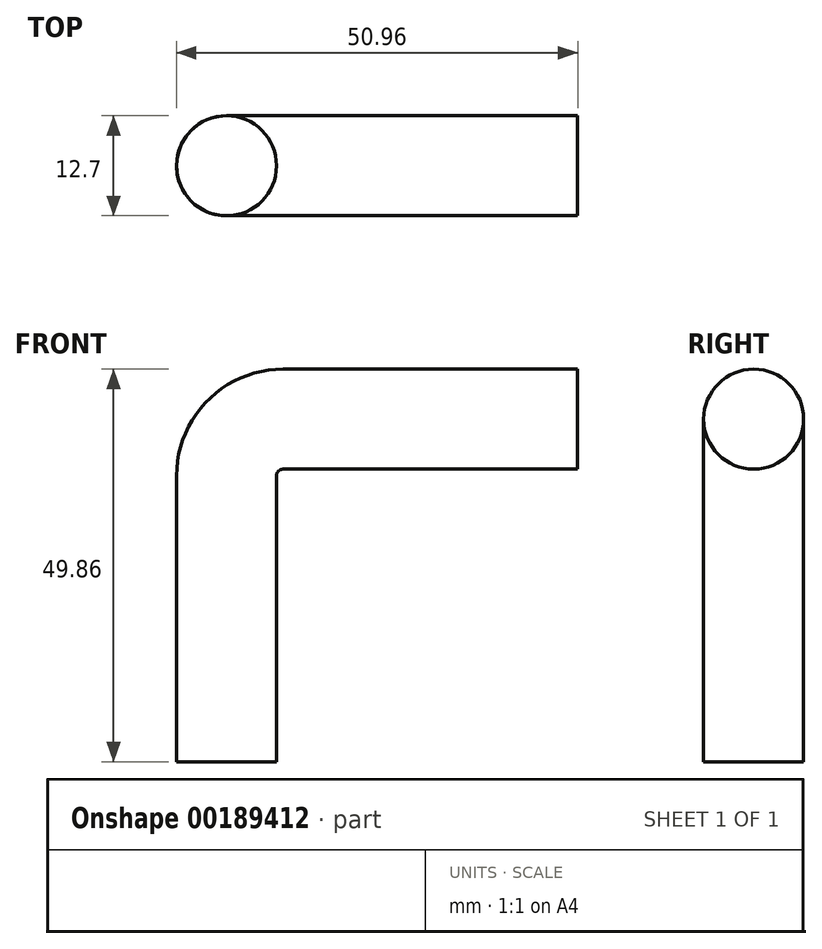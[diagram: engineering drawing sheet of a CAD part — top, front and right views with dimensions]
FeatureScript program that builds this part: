
annotation { "Feature Type Name" : "Feature", "Feature Type Description" : "" }
export const myFeature = defineFeature(function(context is Context, id is Id, definition is map)
    precondition{}
    {
        {
            var Q0;
            Q0=qCreatedBy(makeId("Top.planeOp"),FACE);
            var sketch = newSketch(context, id + "F0", { "sketchPlane" : qUnion([Q0])});
            skCircle(sketch, "E0", {"center": v(0, 0) * mm, "radius": 6.35 * mm});
            skSolve(sketch);
        }
        {
            var Q0;
            Q0=qCreatedBy(makeId("Front.planeOp"),FACE);
            var sketch = newSketch(context, id + "F1", { "sketchPlane" : qUnion([Q0])});
            skLineSegment(sketch, "E1", {"start": v(0, 0) * mm, "end": v(0, 36.34) * mm});
            skLineSegment(sketch, "E2", {"start": v(7.17, 43.51) * mm, "end": v(44.6, 43.51) * mm});
            skArc(sketch, "E3", {"start": v(7.17, 43.51) * mm, "mid": v(2.1, 41.41) * mm, "end": v(0, 36.34) * mm});
            skSolve(sketch);
        }
        {
            var Q0;
            Q0 = qSketchRegion(id + "F0", true);
            var Q1;
            Q1 = qConstructionFilter(qBodyType(qCreatedBy(id + "F1" ,EDGE), BodyType.WIRE), ConstructionObject.NO);
            sweep(context, id + "F2", {"profiles" : qUnion([Q0]), "path" : qUnion([Q1])});
        }
    });
